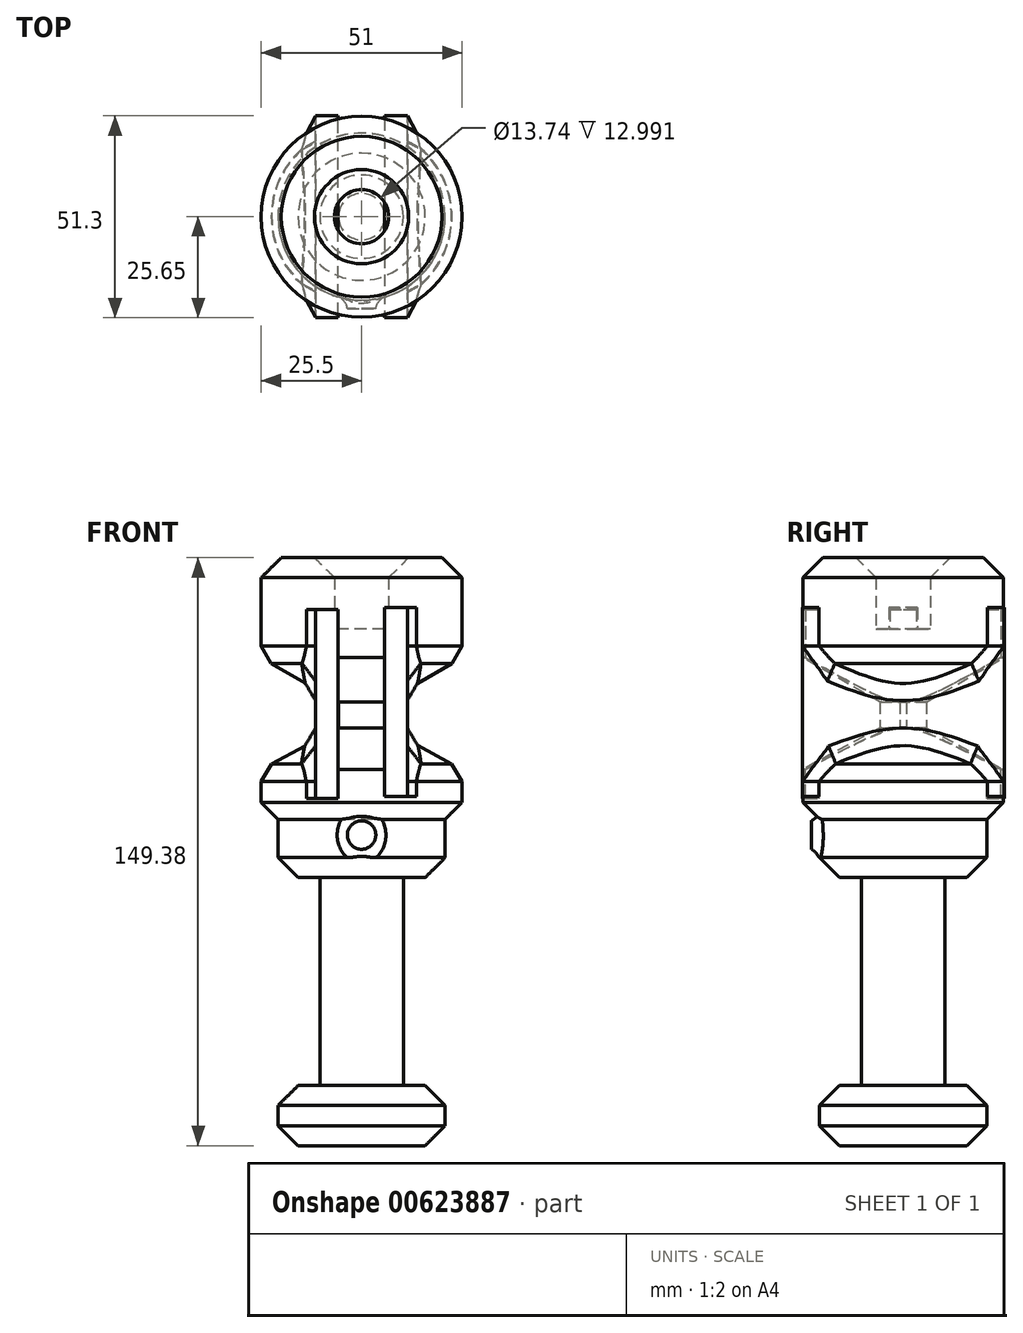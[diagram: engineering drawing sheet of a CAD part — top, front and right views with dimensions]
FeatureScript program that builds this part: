
annotation { "Feature Type Name" : "Feature", "Feature Type Description" : "" }
export const myFeature = defineFeature(function(context is Context, id is Id, definition is map)
    precondition{}
    {
        {
            var Q0;
            Q0=qCreatedBy(makeId("Front.planeOp"),FACE);
            var sketch = newSketch(context, id + "F0", { "sketchPlane" : qUnion([Q0])});
            skLineSegment(sketch, "E0", {"start": v(0, 49.01) * mm, "end": v(-25.5, 49.01) * mm});
            skLineSegment(sketch, "E1", {"start": v(0, 34.36) * mm, "end": v(-25.5, 49.01) * mm});
            skLineSegment(sketch, "E2", {"start": v(0, 49.01) * mm, "end": v(0, 34.36) * mm});
            skLineSegment(sketch, "E3", {"start": v(0, 34.36) * mm, "end": v(-25.5, 20.61) * mm});
            skLineSegment(sketch, "E4", {"start": v(-25.5, 20.61) * mm, "end": v(0, 20.61) * mm});
            skLineSegment(sketch, "E5", {"start": v(0, 20.61) * mm, "end": v(0, 34.36) * mm});
            skLineSegment(sketch, "E6", {"start": v(-6.87, 49.01) * mm, "end": v(-6.87, 56.34) * mm});
            skLineSegment(sketch, "E7", {"start": v(-6.87, 56.34) * mm, "end": v(0, 56.34) * mm});
            skLineSegment(sketch, "E8", {"start": v(0, 56.34) * mm, "end": v(0, 49.01) * mm});
            skLineSegment(sketch, "E9", {"start": v(-6.87, 20.61) * mm, "end": v(-6.87, 7.79) * mm});
            skLineSegment(sketch, "E10", {"start": v(-6.87, 7.79) * mm, "end": v(-21.22, 7.79) * mm});
            skLineSegment(sketch, "E11", {"start": v(-21.22, 7.79) * mm, "end": v(-21.22, -6.87) * mm});
            skLineSegment(sketch, "E12", {"start": v(-21.22, -6.87) * mm, "end": v(0, -6.87) * mm});
            skLineSegment(sketch, "E13", {"start": v(0, -6.87) * mm, "end": v(0, 20.61) * mm});
            skLineSegment(sketch, "E14", {"start": v(-6.87, -6.87) * mm, "end": v(-6.87, -59.7) * mm});
            skLineSegment(sketch, "E15", {"start": v(-21.22, -59.7) * mm, "end": v(-21.22, -74.97) * mm});
            skLineSegment(sketch, "E16", {"start": v(-21.22, -74.97) * mm, "end": v(0, -74.97) * mm});
            skLineSegment(sketch, "E17", {"start": v(0, -74.97) * mm, "end": v(0, -59.7) * mm});
            skLineSegment(sketch, "E18", {"start": v(0, -59.7) * mm, "end": v(-21.22, -59.7) * mm});
            skLineSegment(sketch, "E19", {"start": v(-6.87, -59.7) * mm, "end": v(0, -59.7) * mm});
            skLineSegment(sketch, "E20", {"start": v(0, -6.87) * mm, "end": v(0, -59.7) * mm});
            skLineSegment(sketch, "E21", {"start": v(-5.9, 37.74) * mm, "end": v(-5.9, 31.18) * mm});
            skLineSegment(sketch, "E22", {"start": v(-10.61, -6.87) * mm, "end": v(-10.61, -59.7) * mm});
            skLineSegment(sketch, "E23", {"start": v(-10.61, -59.7) * mm, "end": v(-6.87, -59.7) * mm});
            skLineSegment(sketch, "E24", {"start": v(-6.87, -6.87) * mm, "end": v(-10.61, -6.87) * mm});
            skSolve(sketch);
        }
        {
            var Q0;
            {var subQ2=sQuery(id+"F0.wireOp",EDGE,"E6");Q0=makeQuery(id+"F0.imprint","IMPRINT",FACE,{"disambiguationData":[TD([[makeQuery(id+"F0.imprint","IMPRINT",EDGE,{"derivedFrom":subQ2}),-1.0]])]});}
            var Q1;
            {var subQ3=sQuery(id+"F0.wireOp",EDGE,"E1");Q1=makeQuery(id+"F0.imprint","IMPRINT",FACE,{"disambiguationData":[TD([[makeQuery(id+"F0.imprint","IMPRINT",EDGE,{"derivedFrom":subQ3}),-1.0]])]});}
            var Q2;
            {var subQ0=sQuery(id+"F0.wireOp",EDGE,"E3");Q2=makeQuery(id+"F0.imprint","IMPRINT",FACE,{"disambiguationData":[TD([[makeQuery(id+"F0.imprint","IMPRINT",EDGE,{"derivedFrom":subQ0}),1.0]])]});}
            var Q3;
            {var subQ1=sQuery(id+"F0.wireOp",EDGE,"E9");Q3=makeQuery(id+"F0.imprint","IMPRINT",FACE,{"disambiguationData":[TD([[makeQuery(id+"F0.imprint","IMPRINT",EDGE,{"derivedFrom":subQ1}),1.0]])]});}
            var Q4;
            {var subQ2=sQuery(id+"F0.wireOp",EDGE,"E14");Q4=makeQuery(id+"F0.imprint","IMPRINT",FACE,{"disambiguationData":[TD([[makeQuery(id+"F0.imprint","IMPRINT",EDGE,{"derivedFrom":subQ2}),1.0]])]});}
            var Q5;
            Q5=makeQuery(id+"F0.imprint","IMPRINT",FACE,{"disambiguationData":[TD([[makeQuery(id+"F0.imprint","IMPRINT",EDGE,{"derivedFrom":sQuery(id+"F0.wireOp",EDGE,"E15")}),1.0]])]});
            var Q6;
            {var subQ3=sQuery(id+"F0.wireOp",EDGE,"E21");Q6=makeQuery(id+"F0.imprint","IMPRINT",FACE,{"disambiguationData":[TD([[makeQuery(id+"F0.imprint","IMPRINT",EDGE,{"derivedFrom":subQ3}),1.0]])]});}
            var Q7;
            Q7=makeQuery(id+"F0.imprint","IMPRINT",FACE,{"disambiguationData":[TD([[makeQuery(id+"F0.imprint","IMPRINT",EDGE,{"derivedFrom":sQuery(id+"F0.wireOp",EDGE,"E14")}),-1.0]])]});
            var Q8;
            Q8=sQuery(id+"F0.wireOp",EDGE,"E13");
            revolve(context, id + "F1", {"entities" : qUnion([Q0, Q1, Q2, Q3, Q4, Q5, Q6, Q7]), "axis" : qUnion([Q8]), "revolveType" : RevolveType.FULL});
        }
        {
            var Q0;
            Q0=makeQuery(id+"F1.opRevolve","SWEPT_FACE",FACE,{"disambiguationData":[OSD([sQuery(id+"F0.wireOp",EDGE,"E0")])]});
            extrude(context, id + "F2", {"entities" : qUnion([Q0]), "operationType" : NewBodyOperationType.ADD, "depth" : 25.4 * mm, "offsetDistance" : 25.4 * mm});
        }
        {
            var Q0;
            Q0=makeQuery(id+"F1.opRevolve","SWEPT_FACE",FACE,{"disambiguationData":[OSD([sQuery(id+"F0.wireOp",EDGE,"E4")])]});
            extrude(context, id + "F3", {"entities" : qUnion([Q0]), "operationType" : NewBodyOperationType.ADD, "depth" : 13.46 * mm, "offsetDistance" : 25.4 * mm});
        }
        {
            var Q0;
            Q0=qCreatedBy(makeId("Front.planeOp"),FACE);
            var sketch = newSketch(context, id + "F4", { "sketchPlane" : qUnion([Q0])});
            skLineSegment(sketch, "E25", {"start": v(-5.97, 13.28) * mm, "end": v(-5.97, 61.23) * mm});
            skLineSegment(sketch, "E26", {"start": v(-5.97, 61.23) * mm, "end": v(-11.76, 61.23) * mm});
            skLineSegment(sketch, "E27", {"start": v(-5.97, 13.28) * mm, "end": v(-11.76, 13.28) * mm});
            skLineSegment(sketch, "E28", {"start": v(-11.76, 13.28) * mm, "end": v(-11.76, 61.23) * mm});
            skLineSegment(sketch, "E29", {"start": v(5.83, 61.71) * mm, "end": v(5.83, 13.76) * mm});
            skLineSegment(sketch, "E30", {"start": v(5.83, 13.76) * mm, "end": v(11.62, 13.76) * mm});
            skLineSegment(sketch, "E31", {"start": v(11.62, 13.76) * mm, "end": v(11.62, 61.71) * mm});
            skLineSegment(sketch, "E32", {"start": v(11.62, 61.71) * mm, "end": v(5.83, 61.71) * mm});
            skSolve(sketch);
        }
        {
            var Q0;
            Q0=qSketchRegion(id+"F4",true);
            extrude(context, id + "F5", {"entities" : qUnion([Q0]), "operationType" : NewBodyOperationType.ADD, "endBound" : BoundingType.SYMMETRIC, "depth" : 51.3 * mm, "offsetDistance" : 25.4 * mm});
        }
        {
            var Q0;
            Q0=makeQuery(id+"F1.opRevolve","SWEPT_FACE",FACE,{"disambiguationData":[OSD([sQuery(id+"F0.wireOp",EDGE,"E16")])]});
            var Q1;
            Q1=makeQuery(id+"F1.opRevolve","SWEPT_EDGE",EDGE,{"disambiguationData":[OSD([sQuery(id+"F0.wireOp",EDGE,"E11"),sQuery(id+"F0.wireOp",EDGE,"E12")])]});
            var Q2;
            Q2=makeQuery(id+"F3.opExtrude","CAP_EDGE",EDGE,{"disambiguationData":[OSD([sQuery(id+"F0.wireOp",EDGE,"E3"),sQuery(id+"F0.wireOp",EDGE,"E4")])],"isStart":false});
            var Q3;
            {var subQ0=sQuery(id+"F0.wireOp",EDGE,"E1");Q3=makeQuery(id+"F5.boolean.opBoolean","SPLIT",FACE,{"disambiguationData":[TD([makeQuery(id+"F5.opExtrude","SWEPT_FACE",FACE,{"disambiguationData":[OSD([sQuery(id+"F4.wireOp",EDGE,"E28")])]})])],"derivedFrom":makeQuery(id+"F1.opRevolve","SWEPT_FACE",FACE,{"disambiguationData":[OSD([subQ0])]})});}
            var Q4;
            {var subQ0=sQuery(id+"F0.wireOp",EDGE,"E1");Q4=makeQuery(id+"F5.boolean.opBoolean","SPLIT",FACE,{"disambiguationData":[TD([makeQuery(id+"F5.opExtrude","SWEPT_FACE",FACE,{"disambiguationData":[OSD([sQuery(id+"F4.wireOp",EDGE,"E31")])]})])],"derivedFrom":makeQuery(id+"F1.opRevolve","SWEPT_FACE",FACE,{"disambiguationData":[OSD([subQ0])]})});}
            var Q5;
            {var subQ0=sQuery(id+"F0.wireOp",EDGE,"E3");Q5=makeQuery(id+"F5.boolean.opBoolean","SPLIT",FACE,{"disambiguationData":[TD([makeQuery(id+"F5.opExtrude","SWEPT_FACE",FACE,{"disambiguationData":[OSD([sQuery(id+"F4.wireOp",EDGE,"E28")])]})])],"derivedFrom":makeQuery(id+"F1.opRevolve","SWEPT_FACE",FACE,{"disambiguationData":[OSD([subQ0])]})});}
            var Q6;
            {var subQ0=sQuery(id+"F0.wireOp",EDGE,"E3");Q6=makeQuery(id+"F5.boolean.opBoolean","SPLIT",FACE,{"disambiguationData":[TD([makeQuery(id+"F5.opExtrude","SWEPT_FACE",FACE,{"disambiguationData":[OSD([sQuery(id+"F4.wireOp",EDGE,"E31")])]})])],"derivedFrom":makeQuery(id+"F1.opRevolve","SWEPT_FACE",FACE,{"disambiguationData":[OSD([subQ0])]})});}
            var Q7;
            Q7=makeQuery(id+"F2.opExtrude","CAP_FACE",FACE,{"disambiguationData":[OSD([sQuery(id+"F0.wireOp",EDGE,"E0")])],"isStart":false});
            var Q8;
            Q8=makeQuery(id+"F1.opRevolve","SWEPT_EDGE",EDGE,{"disambiguationData":[OSD([sQuery(id+"F0.wireOp",EDGE,"E15"),sQuery(id+"F0.wireOp",EDGE,"E18")])]});
            chamfer(context, id + "F6", {"entities" : qUnion([Q0, Q1, Q2, Q3, Q4, Q5, Q6, Q7, Q8]), "width" : 5.08 * mm, "tangentPropagation" : true});
        }
        {
            var Q0;
            Q0=qCreatedBy(makeId("Front.planeOp"),FACE);
            var sketch = newSketch(context, id + "F7", { "sketchPlane" : qUnion([Q0])});
            skCircle(sketch, "E33", {"center": v(0, 3.95) * mm, "radius": 3.62 * mm});
            skSolve(sketch);
        }
        {
            var Q0;
            Q0=qSketchRegion(id+"F7",true);
            extrude(context, id + "F8", {"entities" : qUnion([Q0]), "operationType" : NewBodyOperationType.ADD, "depth" : 23.37 * mm, "offsetDistance" : 25.4 * mm});
        }
        {
            var Q0;
            Q0=makeQuery(id+"F8.boolean.opBoolean","INTERSECT",EDGE,{"derivedFrom":[makeQuery(id+"F1.opRevolve","SWEPT_FACE",FACE,{"disambiguationData":[OSD([sQuery(id+"F0.wireOp",EDGE,"E11")])]}),makeQuery(id+"F8.opExtrude","SWEPT_FACE",FACE,{"disambiguationData":[OSD([sQuery(id+"F7.wireOp",EDGE,"E33")])]})]});
            fillet(context, id + "F9", {"entities" : qUnion([Q0]), "radius" : 3.68 * mm, "tangentPropagation" : true, "allowEdgeOverflow" : false});
        }
    });
